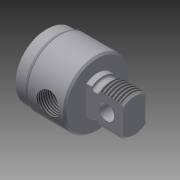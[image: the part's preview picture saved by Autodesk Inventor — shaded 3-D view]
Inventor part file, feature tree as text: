
AUTODESK INVENTOR PART (.ipt)
format: ipt  version: 2014 SP2 (Build 180246200, 246)  size: 291,328 bytes
history: native  units: in
note: dims shown in document units (in); Inventor stores cm internally (conversion verified against a paired STEP export)
features: other x154, sketch x7, revolve x4, thread x2, extrude x2, hole x1
ambient origin geometry x8: Origin, YZ Plane, XZ Plane, XY Plane, X Axis, Y Axis, Z Axis, Center Point
bodies: Solid1 (feature_tree)
feature tree (170):
  revolve  "Revolution1"  Angle=360.0deg
  revolve  "Revolution2"  [1 undecoded]
  thread  "Thread1"  [1 undecoded]
  extrude  "Extrusion1"  TaperAngle=360.0deg  [1 undecoded]
  hole  "Hole1"  [1 undecoded]
  revolve  "Revolution3"  [1 undecoded]
  thread  "Thread2"  [1 undecoded]
  revolve  "Revolution4"  [1 undecoded]
  extrude  "Extrusion2"  [1 undecoded]
  other  "1_XY"
  other  "1_YZ"
  other  "1_ZX"
  other  "1_X"
  other  "1_Y"
  other  "1_Z"
  other  "1_Center"
  other  "c1_XY"
  other  "c1_YZ"
  other  "c1_ZX"
  other  "c1_X"
  other  "c1_Y"
  other  "c1_Z"
  other  "c1_Center"
  other  "c2_XY"
  other  "c2_YZ"
  other  "c2_ZX"
  other  "c2_X"
  other  "c2_Y"
  other  "c2_Z"
  other  "c2_Center"
  other  "cc1_XY"
  other  "cc1_YZ"
  other  "cc1_ZX"
  other  "cc1_X"
  other  "cc1_Y"
  other  "cc1_Z"
  other  "cc1_Center"
  other  "cc2_XY"
  other  "cc2_YZ"
  other  "cc2_ZX"
  other  "cc2_X"
  other  "cc2_Y"
  other  "cc2_Z"
  other  "cc2_Center"
  other  "lovra1_XY"
  other  "lovra1_YZ"
  other  "lovra1_ZX"
  other  "lovra1_X"
  other  "lovra1_Y"
  other  "lovra1_Z"
  other  "lovra1_Center"
  other  "lovra2_XY"
  other  "lovra2_YZ"
  other  "lovra2_ZX"
  other  "lovra2_X"
  other  "lovra2_Y"
  other  "lovra2_Z"
  other  "lovra2_Center"
  other  "lovra21_XY"
  other  "lovra21_YZ"
  other  "lovra21_ZX"
  other  "lovra21_X"
  other  "lovra21_Y"
  other  "lovra21_Z"
  other  "lovra21_Center"
  other  "lovra22_XY"
  other  "lovra22_YZ"
  other  "lovra22_ZX"
  other  "lovra22_X"
  other  "lovra22_Y"
  other  "lovra22_Z"
  other  "lovra22_Center"
  other  "lovra3_XY"
  other  "lovra3_YZ"
  other  "lovra3_ZX"
  other  "lovra3_X"
  other  "lovra3_Y"
  other  "lovra3_Z"
  other  "lovra3_Center"
  other  "olen_XY"
  other  "olen_YZ"
  other  "olen_ZX"
  other  "olen_X"
  other  "olen_Y"
  other  "olen_Z"
  other  "olen_Center"
  other  "p1_XY"
  other  "p1_YZ"
  other  "p1_ZX"
  other  "p1_X"
  other  "p1_Y"
  other  "p1_Z"
  other  "p1_Center"
  other  "p2_XY"
  other  "p2_YZ"
  other  "p2_ZX"
  other  "p2_X"
  other  "p2_Y"
  other  "p2_Z"
  other  "p2_Center"
  other  "port_XY"
  other  "port_YZ"
  other  "port_ZX"
  other  "port_X"
  other  "port_Y"
  other  "port_Z"
  other  "port_Center"
  other  "port2_XY"
  other  "port2_YZ"
  other  "port2_ZX"
  other  "port2_X"
  other  "port2_Y"
  other  "port2_Z"
  other  "port2_Center"
  other  "thd1_XY"
  other  "thd1_YZ"
  other  "thd1_ZX"
  other  "thd1_X"
  other  "thd1_Y"
  other  "thd1_Z"
  other  "thd1_Center"
  other  "thd2_XY"
  other  "thd2_YZ"
  other  "thd2_ZX"
  other  "thd2_X"
  other  "thd2_Y"
  other  "thd2_Z"
  other  "thd2_Center"
  other  "to_mounting_bracket_XY"
  other  "to_mounting_bracket_YZ"
  other  "to_mounting_bracket_ZX"
  other  "to_mounting_bracket_X"
  other  "to_mounting_bracket_Y"
  other  "to_mounting_bracket_Z"
  other  "to_mounting_bracket_Center"
  other  "to_nut_XY"
  other  "to_nut_YZ"
  other  "to_nut_ZX"
  other  "to_nut_X"
  other  "to_nut_Y"
  other  "to_nut_Z"
  other  "to_nut_Center"
  other  "to_pin_XY"
  other  "to_pin_YZ"
  other  "to_pin_ZX"
  other  "to_pin_X"
  other  "to_pin_Y"
  other  "to_pin_Z"
  other  "to_pin_Center"
  other  "to_screw_XY"
  other  "to_screw_YZ"
  other  "to_screw_ZX"
  other  "to_screw_X"
  other  "to_screw_Y"
  other  "to_screw_Z"
  other  "to_screw_Center"
  other  "to_tube_XY"
  other  "to_tube_YZ"
  other  "to_tube_ZX"
  other  "to_tube_X"
  other  "to_tube_Y"
  other  "to_tube_Z"
  other  "to_tube_Center"
  sketch  "Sketch_18"  dims[d14=0.2731in d15=0.0in d16=360.0deg]
  sketch  "Sketch_15"  dims[d6=0.375in d7=0.75in d8=0.375in d9=0.25in d10=0.5635in d11=0.825in d12=120.0deg d13=360.0deg]
  sketch  "Sketch_9"  dims[d2=0.3547in d3=0.0in d4=0.625in d5=0.0in]
  sketch  "Sketch4"  dims[d0=360.0deg d1=360.0deg]
  sketch  "Sketch_68"
  sketch  "Sketch_24"  dims[d17=0.5587in d18=0.0in]
  sketch  "Sketch_43"  dims[d19=0.0in d20=0.0in d21=0.0in d22=0.0in d23=0.0in d24=0.0in d25=0.0in d26=0.0in]
note: 8 required parameter values undecoded (feature->parameter linkage not recoverable at this tier; creation-order binding heuristic only, values carry confidence <= 0.55)